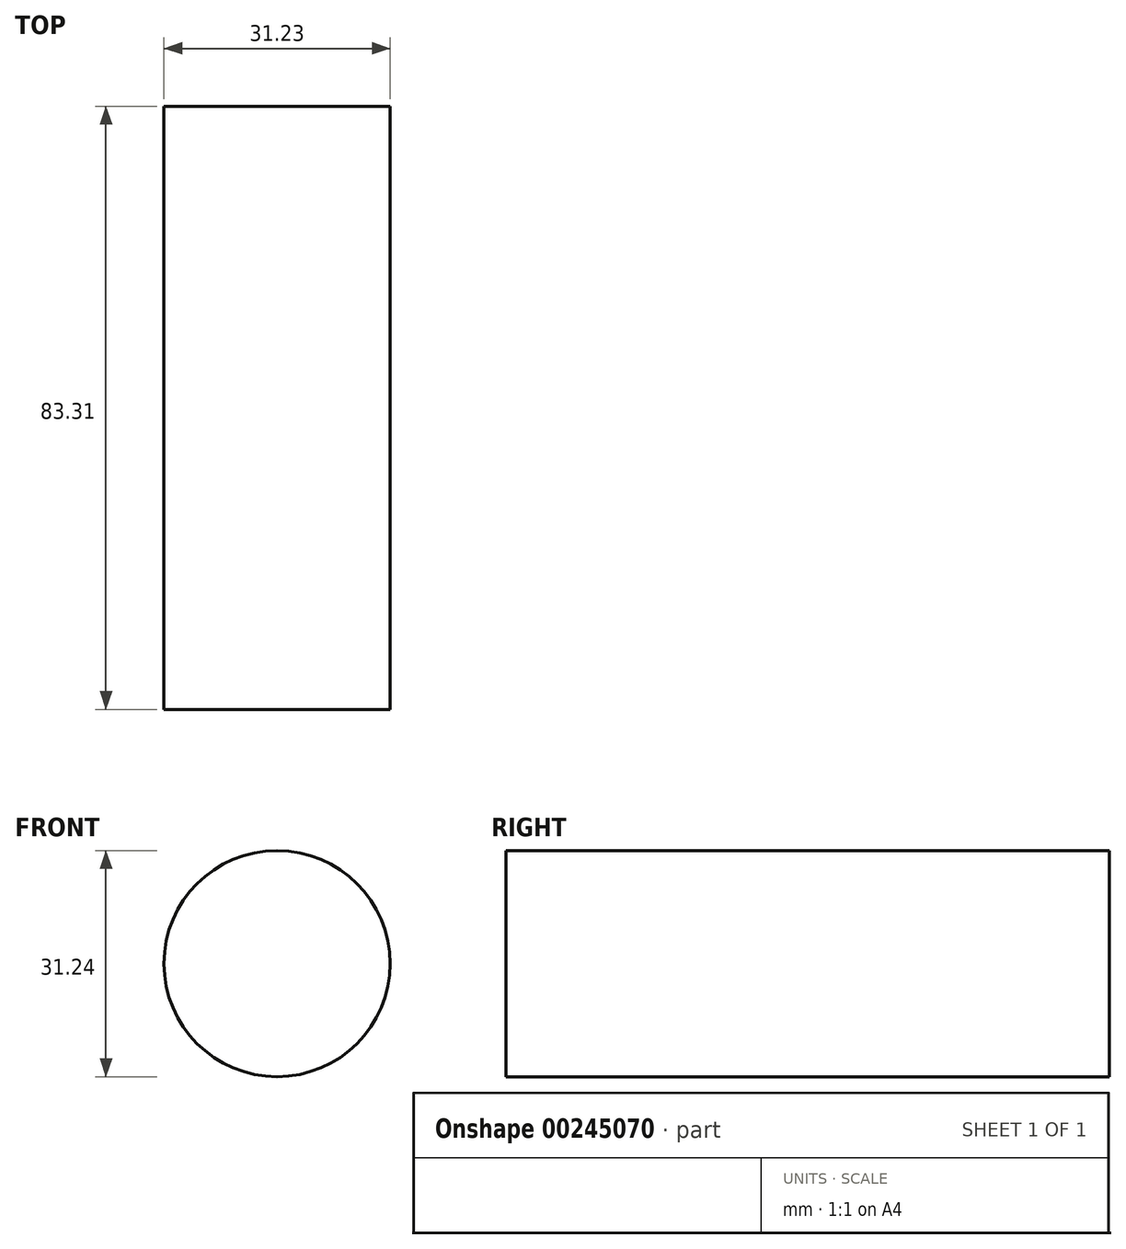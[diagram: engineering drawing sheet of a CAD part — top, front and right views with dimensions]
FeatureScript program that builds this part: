
annotation { "Feature Type Name" : "Feature", "Feature Type Description" : "" }
export const myFeature = defineFeature(function(context is Context, id is Id, definition is map)
    precondition{}
    {
        {
            var Q0;
            Q0=qCreatedBy(makeId("Front.planeOp"),FACE);
            var sketch = newSketch(context, id + "F0", { "sketchPlane" : qUnion([Q0])});
            skCircle(sketch, "E0", {"center": v(-0.08, 0) * mm, "radius": 15.62 * mm});
            skPoint(sketch, "E0.first.point", {"position": v(0, 15.62) * mm});
            skPoint(sketch, "E0.second.point", {"position": v(0, -15.62) * mm});
            skPoint(sketch, "E0.third.point", {"position": v(15.54, 0) * mm});
            skSolve(sketch);
        }
        {
            var Q0;
            Q0=makeQuery(id+"F0.imprint","IMPRINT",FACE,{"disambiguationData":[TD([[makeQuery(id+"F0.imprint","IMPRINT",EDGE,{"derivedFrom":sQuery(id+"F0.wireOp",EDGE,"E0")}),1.0]])]});
            extrude(context, id + "F1", {"entities" : qUnion([Q0]), "oppositeDirection" : true, "depth" : 83.31 * mm});
        }
    });
